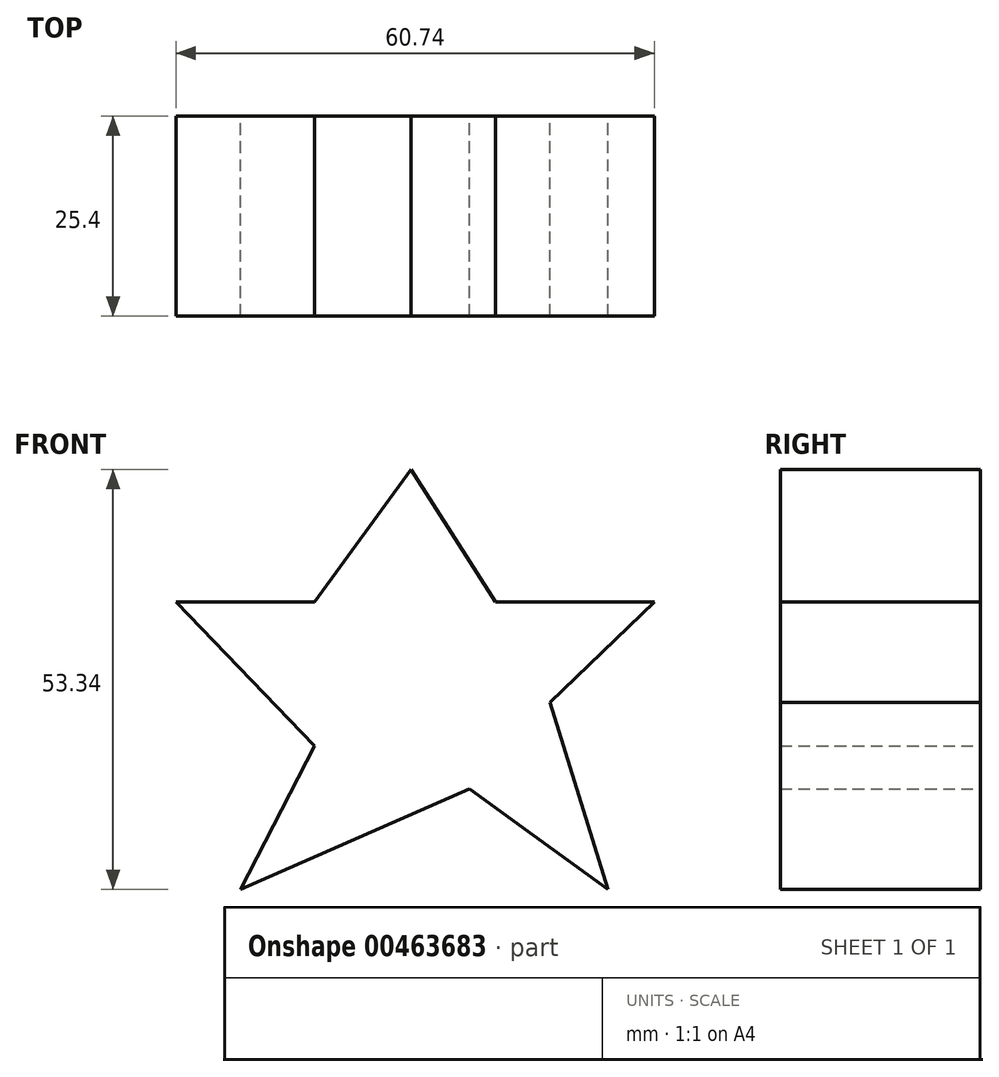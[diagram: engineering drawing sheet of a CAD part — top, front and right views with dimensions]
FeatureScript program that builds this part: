
annotation { "Feature Type Name" : "Feature", "Feature Type Description" : "" }
export const myFeature = defineFeature(function(context is Context, id is Id, definition is map)
    precondition{}
    {
        {
            var Q0;
            Q0=qCreatedBy(makeId("Front.planeOp"),FACE);
            var sketch = newSketch(context, id + "F0", { "sketchPlane" : qUnion([Q0])});
            skLineSegment(sketch, "E0", {"start": v(10.08, -13.9) * mm, "end": v(18.25, -19.78) * mm});
            skLineSegment(sketch, "E1", {"start": v(18.25, -19.78) * mm, "end": v(27.7, -26.67) * mm});
            skLineSegment(sketch, "E2", {"start": v(27.7, -26.67) * mm, "end": v(20.29, -2.93) * mm});
            skLineSegment(sketch, "E3", {"start": v(20.29, -2.93) * mm, "end": v(33.56, 9.83) * mm});
            skLineSegment(sketch, "E4", {"start": v(33.56, 9.83) * mm, "end": v(13.4, 9.83) * mm});
            skLineSegment(sketch, "E5", {"start": v(13.4, 9.83) * mm, "end": v(2.68, 26.67) * mm});
            skLineSegment(sketch, "E6", {"start": v(2.68, 26.67) * mm, "end": v(-9.61, 9.83) * mm});
            skLineSegment(sketch, "E7", {"start": v(-9.61, 9.83) * mm, "end": v(-27.18, 9.83) * mm});
            skLineSegment(sketch, "E8", {"start": v(-27.18, 9.83) * mm, "end": v(-9.61, -8.45) * mm});
            skLineSegment(sketch, "E9", {"start": v(-9.61, -8.45) * mm, "end": v(-19.01, -26.67) * mm});
            skLineSegment(sketch, "E10", {"start": v(10.08, -13.9) * mm, "end": v(-19.01, -26.67) * mm});
            skSolve(sketch);
        }
        {
            var Q0;
            Q0 = qSketchRegion(id + "F0", true);
            extrude(context, id + "F1", {"entities" : qUnion([Q0]), "depth" : 25.4 * mm});
        }
    });
